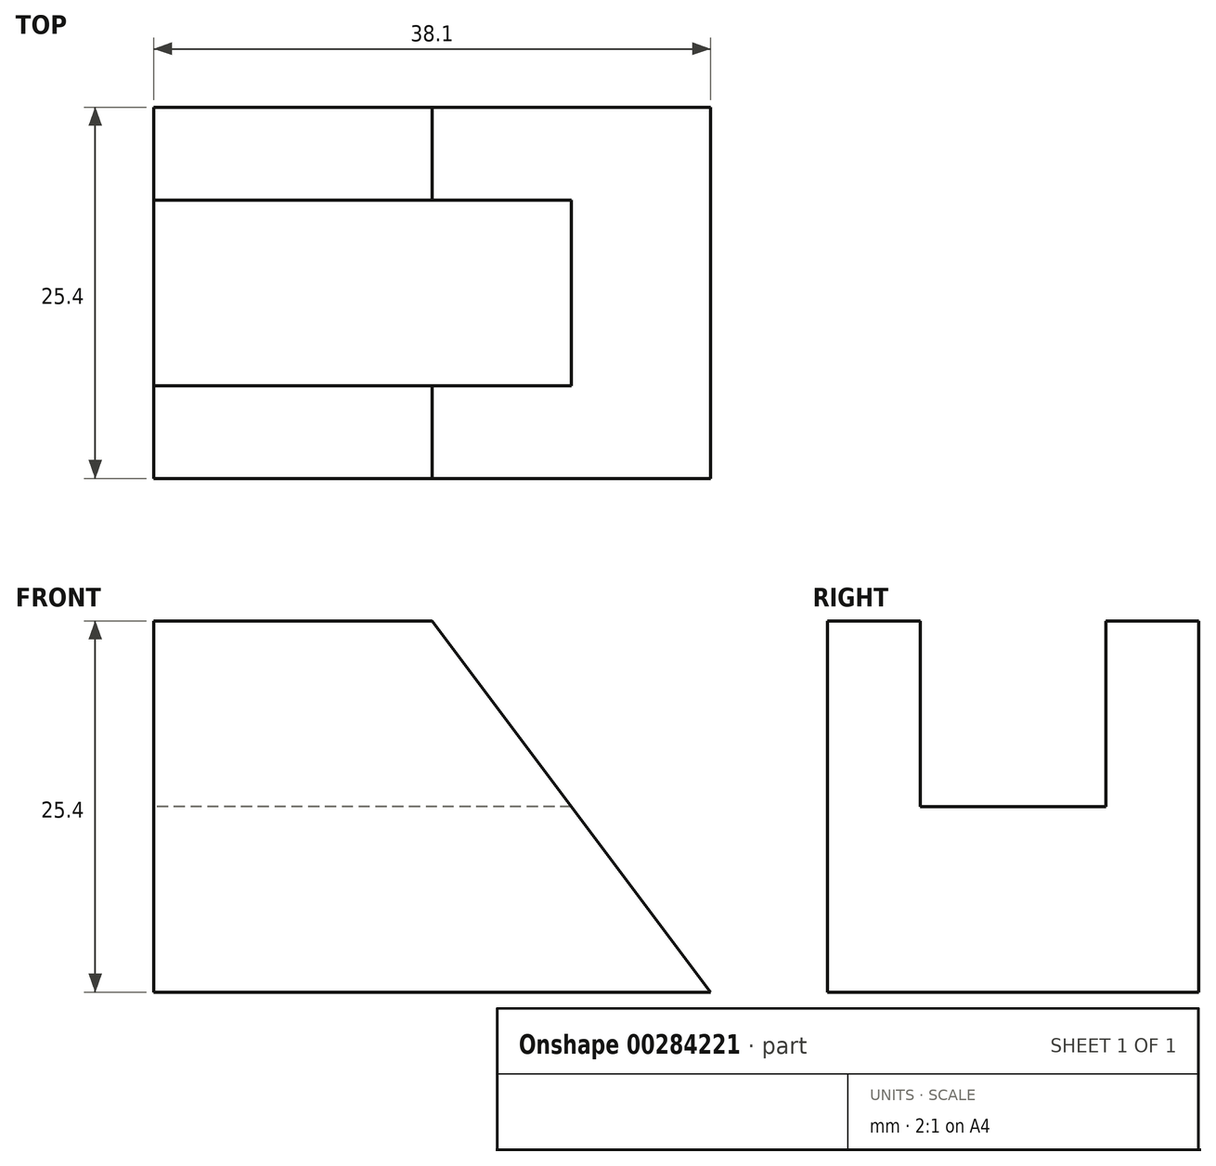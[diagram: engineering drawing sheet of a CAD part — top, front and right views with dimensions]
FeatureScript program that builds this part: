
annotation { "Feature Type Name" : "Feature", "Feature Type Description" : "" }
export const myFeature = defineFeature(function(context is Context, id is Id, definition is map)
    precondition{}
    {
        {
            var Q0;
            Q0=qCreatedBy(makeId("Front.planeOp"),FACE);
            var sketch = newSketch(context, id + "F0", { "sketchPlane" : qUnion([Q0])});
            skLineSegment(sketch, "E0", {"start": v(0, 0) * mm, "end": v(0, 25.4) * mm});
            skLineSegment(sketch, "E1", {"start": v(0, 25.4) * mm, "end": v(19.05, 25.4) * mm});
            skLineSegment(sketch, "E2", {"start": v(19.05, 25.4) * mm, "end": v(38.1, 0) * mm});
            skLineSegment(sketch, "E3", {"start": v(38.1, 0) * mm, "end": v(0, 0) * mm});
            skSolve(sketch);
        }
        {
            var Q0;
            Q0=makeQuery(id+"F0.imprint","IMPRINT",FACE,{"disambiguationData":[TD([[makeQuery(id+"F0.imprint","IMPRINT",EDGE,{"derivedFrom":sQuery(id+"F0.wireOp",EDGE,"E0")}),-1.0]])]});
            extrude(context, id + "F1", {"entities" : qUnion([Q0]), "depth" : 25.4 * mm});
        }
        {
            var Q0;
            Q0=makeQuery(id+"F1.opExtrude","SWEPT_FACE",FACE,{"disambiguationData":[OSD([sQuery(id+"F0.wireOp",EDGE,"E0")])]});
            var sketch = newSketch(context, id + "F2", { "sketchPlane" : qUnion([Q0])});
            skLineSegment(sketch, "E4", {"start": v(6.35, 25.4) * mm, "end": v(6.35, 12.7) * mm});
            skLineSegment(sketch, "E5", {"start": v(6.35, 12.7) * mm, "end": v(19.05, 12.7) * mm});
            skLineSegment(sketch, "E6", {"start": v(19.05, 12.7) * mm, "end": v(19.05, 25.4) * mm});
            skLineSegment(sketch, "E7", {"start": v(19.05, 25.4) * mm, "end": v(6.35, 25.4) * mm});
            skSolve(sketch);
        }
        {
            var Q0;
            Q0=makeQuery(id+"F2.imprint","IMPRINT",FACE,{"disambiguationData":[TD([[makeQuery(id+"F2.imprint","IMPRINT",EDGE,{"derivedFrom":sQuery(id+"F2.wireOp",EDGE,"E4")}),1.0]])]});
            extrude(context, id + "F3", {"entities" : qUnion([Q0]), "operationType" : NewBodyOperationType.REMOVE, "oppositeDirection" : true, "depth" : 38.1 * mm});
        }
    });
